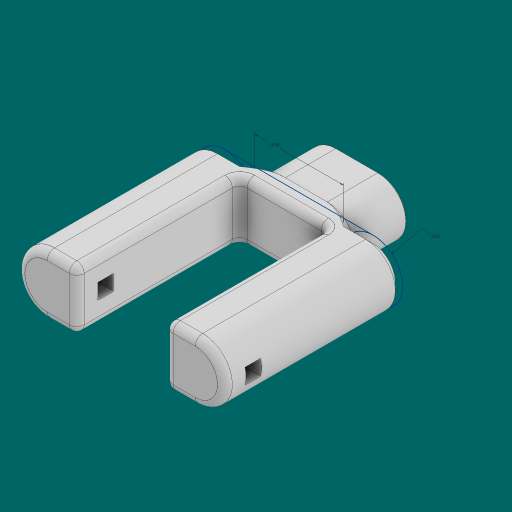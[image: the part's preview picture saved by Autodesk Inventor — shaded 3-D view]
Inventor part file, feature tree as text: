
AUTODESK INVENTOR PART (.ipt)
format: ipt  version: 2023.1 (Build 271208000, 208)  size: 514,560 bytes
history: native  units: in
note: dims shown in document units (in); Inventor stores cm internally (conversion verified against a paired STEP export)
features: extrude x4, sketch x3, fillet x3, chamfer x3
ambient origin geometry x8: Origin, YZ Plane, XZ Plane, XY Plane, X Axis, Y Axis, Z Axis, Center Point
bodies: Solid1 (feature_tree)
feature tree (13):
  extrude  "Extrusion1"  Depth=0.25in TaperAngle=0.0deg
  sketch  "Sketch2"  dims[d4=3.0in d5=0.0in d6=0.26in]
  extrude  "Extrusion2"  Depth=0.26in
  extrude  "Extrusion3"  TaperAngle=0.0deg  [1 undecoded]
  extrude  "Extrusion4"  Depth=0.4724in
  fillet  "Fillet1"  Radius=0.4724in
  fillet  "Fillet2"  Radius=0.7087in
  fillet  "Fillet3"  Radius=1.5in
  chamfer  "Chamfer1"  Distance=0.125in
  chamfer  "Chamfer2"  Distance=0.125in
  chamfer  "Chamfer3"  Distance=0.125in
  sketch  "Sketch1"  dims[d0=1.0in d1=0.0in d2=0.25in d3=0.0in]
  sketch  "Sketch3"  dims[d7=0.26in d8=0.0in d9=0.0in d10=0.5in d11=0.4724in d12=0.7087in d13=1.5in d14=0.125in d15=0.125in d16=0.125in d17=0.125in d18=0.125in d19=45.0deg d20=0.125in d21=0.125in d22=45.0deg d23=0.0236in d24=0.125in d25=45.0deg]
note: 1 required parameter value undecoded (feature->parameter linkage not recoverable at this tier; creation-order binding heuristic only, values carry confidence <= 0.55)
